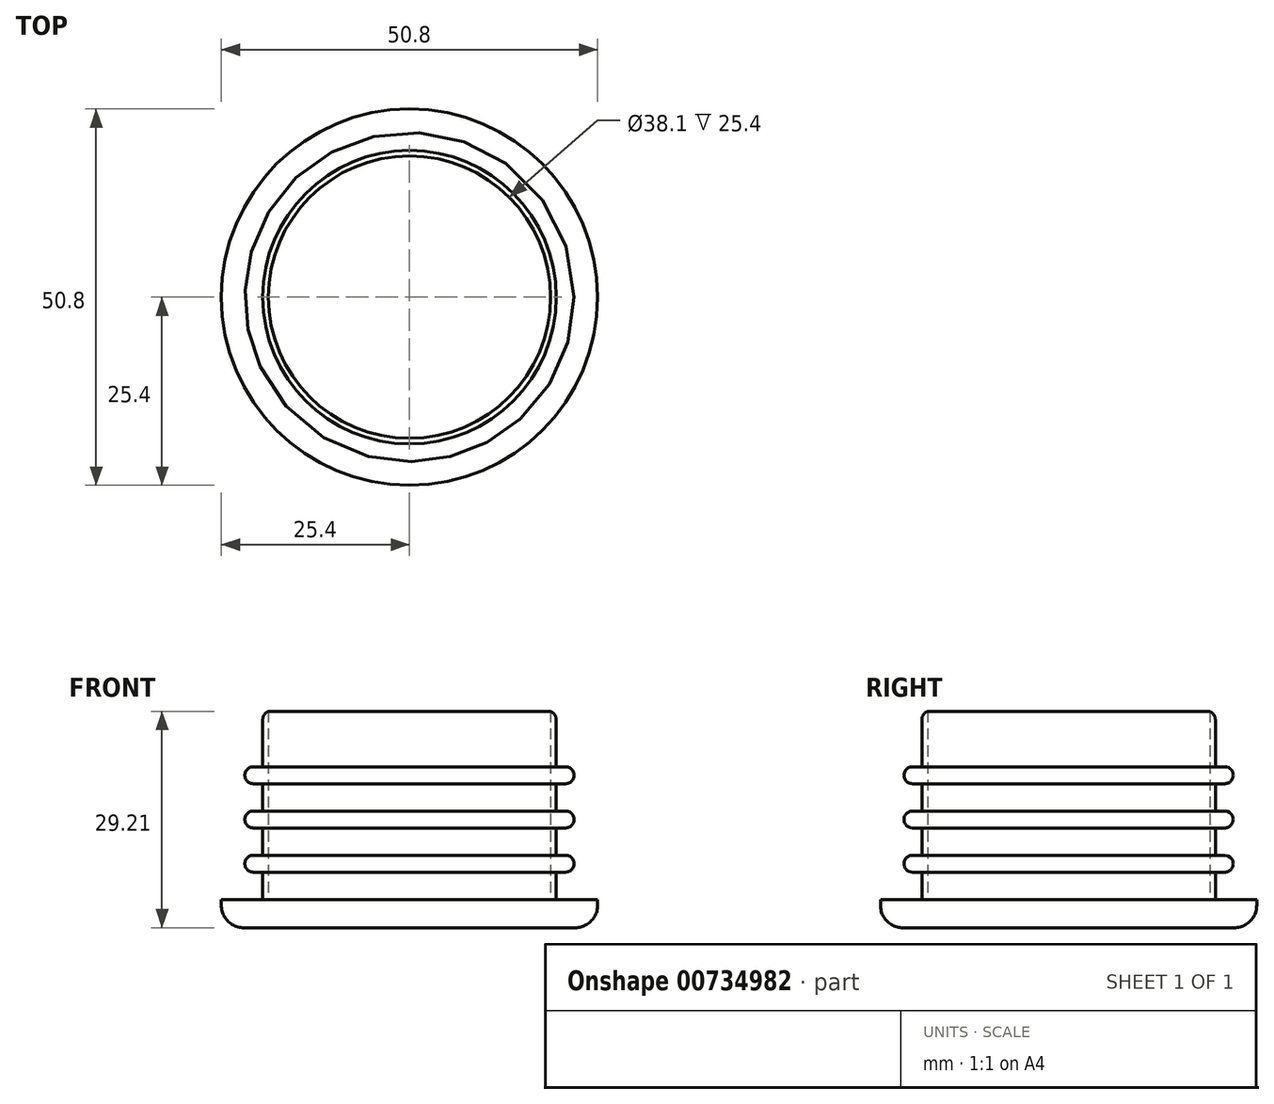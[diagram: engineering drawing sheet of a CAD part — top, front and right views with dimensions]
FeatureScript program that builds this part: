
annotation { "Feature Type Name" : "Feature", "Feature Type Description" : "" }
export const myFeature = defineFeature(function(context is Context, id is Id, definition is map)
    precondition{}
    {
        {
            var Q0;
            Q0=qCreatedBy(makeId("Top.planeOp"),FACE);
            var sketch = newSketch(context, id + "F0", { "sketchPlane" : qUnion([Q0])});
            skCircle(sketch, "E0", {"center": v(0, 0) * mm, "radius": 19.05 * mm});
            skCircle(sketch, "E1", {"center": v(0, 0) * mm, "radius": 25.4 * mm});
            skCircle(sketch, "E2", {"center": v(0, 0) * mm, "radius": 19.81 * mm});
            skSolve(sketch);
        }
        {
            var Q0;
            Q0=makeQuery(id+"F0.imprint","IMPRINT",FACE,{"disambiguationData":[TD([[makeQuery(id+"F0.imprint","IMPRINT",EDGE,{"derivedFrom":sQuery(id+"F0.wireOp",EDGE,"E0")}),-1.0]])]});
            extrude(context, id + "F1", {"entities" : qUnion([Q0]), "depth" : 29.2 * mm, "offsetDistance" : 25.4 * mm});
        }
        {
            var Q0;
            Q0=makeQuery(id+"F0.imprint","IMPRINT",FACE,{"disambiguationData":[TD([[makeQuery(id+"F0.imprint","IMPRINT",EDGE,{"derivedFrom":sQuery(id+"F0.wireOp",EDGE,"E0")}),1.0]])]});
            var Q1;
            Q1=makeQuery(id+"F0.imprint","IMPRINT",FACE,{"disambiguationData":[TD([[makeQuery(id+"F0.imprint","IMPRINT",EDGE,{"derivedFrom":sQuery(id+"F0.wireOp",EDGE,"E1")}),1.0]])]});
            var Q2;
            Q2=makeQuery(id+"F0.imprint","IMPRINT",FACE,{"disambiguationData":[TD([[makeQuery(id+"F0.imprint","IMPRINT",EDGE,{"derivedFrom":sQuery(id+"F0.wireOp",EDGE,"E0")}),-1.0]])]});
            extrude(context, id + "F2", {"entities" : qUnion([Q0, Q1, Q2]), "operationType" : NewBodyOperationType.ADD, "depth" : 3.8 * mm, "offsetDistance" : 25.4 * mm});
        }
        {
            var Q0;
            Q0=makeQuery(id+"F2.boolean.opBoolean","SPLIT",FACE,{"disambiguationData":[TD([makeQuery(id+"F1.opExtrude","SWEPT_FACE",FACE,{"disambiguationData":[OSD([sQuery(id+"F0.wireOp",EDGE,"E0")])]})])],"derivedFrom":makeQuery(id+"F2.opExtrude","CAP_FACE",FACE,{"disambiguationData":[OSD([sQuery(id+"F0.wireOp",EDGE,"E1")])],"isStart":false})});
            cPlane(context, id + "F3", {"entities" : qUnion([Q0]), "cplaneType" : CPlaneType.OFFSET, "offset" : 4.83 * mm, "width" : 152.4 * mm, "height" : 152.4 * mm});
        }
        {
            var Q0;
            Q0=qCreatedBy(id+"F3.planeOp",FACE);
            cPlane(context, id + "F4", {"entities" : qUnion([Q0]), "cplaneType" : CPlaneType.OFFSET, "offset" : 5.97 * mm, "width" : 152.4 * mm, "height" : 152.4 * mm});
        }
        {
            var Q0;
            Q0=qCreatedBy(id+"F4.planeOp",FACE);
            cPlane(context, id + "F5", {"entities" : qUnion([Q0]), "cplaneType" : CPlaneType.OFFSET, "offset" : 5.97 * mm, "width" : 152.4 * mm, "height" : 152.4 * mm});
        }
        {
            var Q0;
            Q0=qCreatedBy(id+"F3.planeOp",FACE);
            var sketch = newSketch(context, id + "F6", { "sketchPlane" : qUnion([Q0])});
            skCircle(sketch, "E3", {"center": v(0, 0) * mm, "radius": 22.23 * mm});
            skCircle(sketch, "E4", {"center": v(0, 0) * mm, "radius": 19.05 * mm});
            skSolve(sketch);
        }
        {
            var Q0;
            Q0=qCreatedBy(id+"F4.planeOp",FACE);
            var sketch = newSketch(context, id + "F7", { "sketchPlane" : qUnion([Q0])});
            skCircle(sketch, "E5", {"center": v(0, 0) * mm, "radius": 22.23 * mm});
            skCircle(sketch, "E6", {"center": v(0, 0) * mm, "radius": 19.05 * mm});
            skSolve(sketch);
        }
        {
            var Q0;
            Q0=qCreatedBy(id+"F5.planeOp",FACE);
            var sketch = newSketch(context, id + "F8", { "sketchPlane" : qUnion([Q0])});
            skCircle(sketch, "E7", {"center": v(0, 0) * mm, "radius": 22.23 * mm});
            skCircle(sketch, "E8", {"center": v(0, 0) * mm, "radius": 19.05 * mm});
            skSolve(sketch);
        }
        {
            var Q0;
            Q0=makeQuery(id+"F6.imprint","IMPRINT",FACE,{"disambiguationData":[TD([[makeQuery(id+"F6.imprint","IMPRINT",EDGE,{"derivedFrom":sQuery(id+"F6.wireOp",EDGE,"E3")}),1.0]])]});
            extrude(context, id + "F9", {"entities" : qUnion([Q0]), "operationType" : NewBodyOperationType.ADD, "depth" : 2.3 * mm, "offsetDistance" : 25.4 * mm, "symmetric" : true});
        }
        {
            var Q0;
            Q0=makeQuery(id+"F7.imprint","IMPRINT",FACE,{"disambiguationData":[TD([[makeQuery(id+"F7.imprint","IMPRINT",EDGE,{"derivedFrom":sQuery(id+"F7.wireOp",EDGE,"E5")}),1.0]])]});
            extrude(context, id + "F10", {"entities" : qUnion([Q0]), "operationType" : NewBodyOperationType.ADD, "depth" : 2.3 * mm, "offsetDistance" : 25.4 * mm, "symmetric" : true});
        }
        {
            var Q0;
            Q0=makeQuery(id+"F8.imprint","IMPRINT",FACE,{"disambiguationData":[TD([[makeQuery(id+"F8.imprint","IMPRINT",EDGE,{"derivedFrom":sQuery(id+"F8.wireOp",EDGE,"E7")}),1.0]])]});
            extrude(context, id + "F11", {"entities" : qUnion([Q0]), "operationType" : NewBodyOperationType.ADD, "depth" : 2.3 * mm, "offsetDistance" : 25.4 * mm, "symmetric" : true});
        }
        {
            var Q0;
            Q0=makeQuery(id+"F2.opExtrude","CAP_EDGE",EDGE,{"disambiguationData":[OSD([sQuery(id+"F0.wireOp",EDGE,"E1")])],"isStart":true});
            fillet(context, id + "F12", {"entities" : qUnion([Q0]), "radius" : 3.05 * mm, "tangentPropagation" : true, "allowEdgeOverflow" : false});
        }
        {
            var Q0;
            Q0=makeQuery(id+"F1.opExtrude","CAP_EDGE",EDGE,{"disambiguationData":[OSD([sQuery(id+"F0.wireOp",EDGE,"E2")])],"isStart":false});
            fillet(context, id + "F13", {"entities" : qUnion([Q0]), "radius" : 1.27 * mm, "tangentPropagation" : true, "allowEdgeOverflow" : false});
        }
        {
            var Q0;
            Q0=makeQuery(id+"F9.opExtrude","CAP_EDGE",EDGE,{"disambiguationData":[OSD([sQuery(id+"F6.wireOp",EDGE,"E3")])],"isStart":true});
            var Q1;
            Q1=makeQuery(id+"F9.opExtrude","CAP_EDGE",EDGE,{"disambiguationData":[OSD([sQuery(id+"F6.wireOp",EDGE,"E3")])],"isStart":false});
            fillet(context, id + "F14", {"entities" : qUnion([Q0, Q1]), "radius" : 1.14 * mm, "tangentPropagation" : true, "allowEdgeOverflow" : false});
        }
        {
            var Q0;
            Q0=makeQuery(id+"F10.opExtrude","CAP_EDGE",EDGE,{"disambiguationData":[OSD([sQuery(id+"F7.wireOp",EDGE,"E5")])],"isStart":true});
            var Q1;
            Q1=makeQuery(id+"F10.opExtrude","CAP_EDGE",EDGE,{"disambiguationData":[OSD([sQuery(id+"F7.wireOp",EDGE,"E5")])],"isStart":false});
            fillet(context, id + "F15", {"entities" : qUnion([Q0, Q1]), "radius" : 1.14 * mm, "tangentPropagation" : true, "allowEdgeOverflow" : false});
        }
        {
            var Q0;
            Q0=makeQuery(id+"F11.opExtrude","CAP_EDGE",EDGE,{"disambiguationData":[OSD([sQuery(id+"F8.wireOp",EDGE,"E7")])],"isStart":true});
            var Q1;
            Q1=makeQuery(id+"F11.opExtrude","CAP_EDGE",EDGE,{"disambiguationData":[OSD([sQuery(id+"F8.wireOp",EDGE,"E7")])],"isStart":false});
            fillet(context, id + "F16", {"entities" : qUnion([Q0, Q1]), "radius" : 1.14 * mm, "tangentPropagation" : true, "allowEdgeOverflow" : false});
        }
    });
